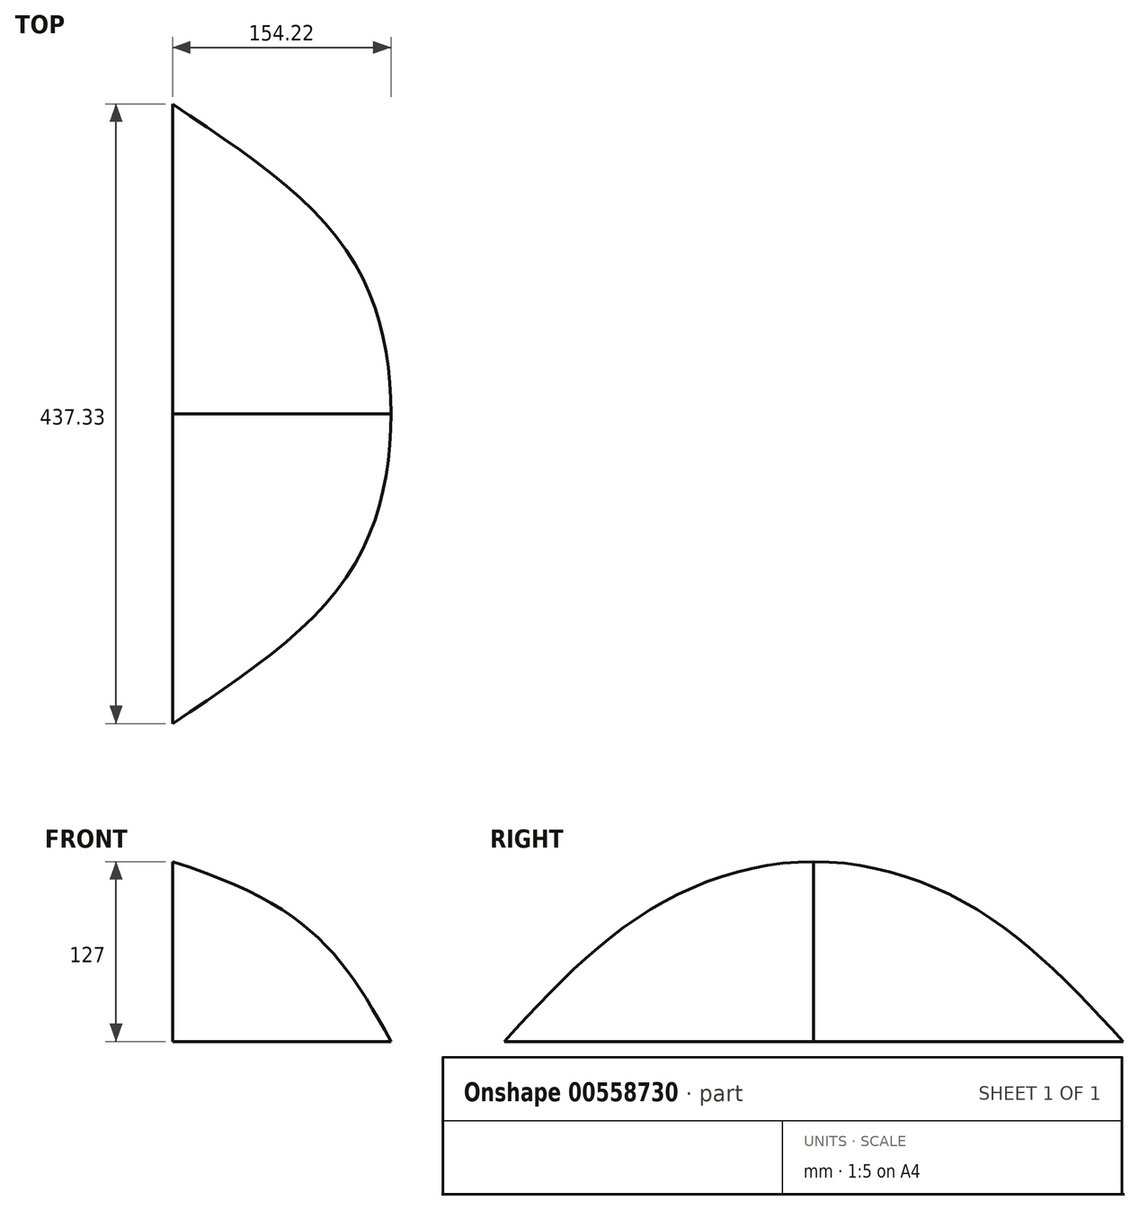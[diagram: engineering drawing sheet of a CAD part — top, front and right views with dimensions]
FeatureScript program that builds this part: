
annotation { "Feature Type Name" : "Feature", "Feature Type Description" : "" }
export const myFeature = defineFeature(function(context is Context, id is Id, definition is map)
    precondition{}
    {
        {
            var Q0;
            Q0=qCreatedBy(makeId("Top.planeOp"),FACE);
            var sketch = newSketch(context, id + "F0", { "sketchPlane" : qUnion([Q0])});
            skFitSpline(sketch, "E0", {"points": [v(0, 174.94) * mm, v(115.82, 81.22) * mm, v(154.22, -43.73) * mm], "startDerivative": vector(281.66, -68.02) * mm, "endDerivative": vector(-8.42, -224.14) * mm});
            skSolve(sketch);
        }
        {
            var Q0;
            Q0=qCreatedBy(makeId("Front.planeOp"),FACE);
            var Q1;
            Q1=sQuery(id+"F0.wireOp",VERTEX,"E0.end");
            cPlane(context, id + "F1", {"entities" : qUnion([Q0, Q1]), "cplaneType" : CPlaneType.PLANE_POINT, "offset" : 25.4 * mm, "width" : 152.4 * mm, "height" : 152.4 * mm});
        }
        {
            var Q0;
            Q0=qCreatedBy(id+"F1.planeOp",FACE);
            var sketch = newSketch(context, id + "F2", { "sketchPlane" : qUnion([Q0])});
            skLineSegment(sketch, "E1", {"start": v(154.22, 0) * mm, "end": v(0, 0) * mm});
            skLineSegment(sketch, "E2", {"start": v(0, 0) * mm, "end": v(0, 127) * mm});
            skFitSpline(sketch, "E3", {"points": [v(0, 127) * mm, v(154.22, 0) * mm], "startDerivative": vector(285.84, -90.22) * mm, "endDerivative": vector(103.03, -188.07) * mm});
            skSolve(sketch);
        }
        {
            var Q0;
            Q0=sQuery(id+"F0.wireOp",VERTEX,"E0.1.internal");
            var Q1;
            Q1=qCreatedBy(id+"F1.planeOp",FACE);
            cPlane(context, id + "F3", {"entities" : qUnion([Q0, Q1]), "cplaneType" : CPlaneType.PLANE_POINT, "offset" : 25.4 * mm, "width" : 152.4 * mm, "height" : 152.4 * mm});
        }
        {
            var Q0;
            Q0=qCreatedBy(makeId("Right.planeOp"),FACE);
            var sketch = newSketch(context, id + "F4", { "sketchPlane" : qUnion([Q0])});
            skFitSpline(sketch, "E4", {"points": [v(174.94, 0) * mm, v(-43.73, 127) * mm], "startDerivative": vector(-117.74, 161.24) * mm, "endDerivative": vector(-284.9, 0) * mm});
            skSolve(sketch);
        }
        {
            var Q0;
            Q0=qCreatedBy(id+"F3.planeOp",FACE);
            var sketch = newSketch(context, id + "F5", { "sketchPlane" : qUnion([Q0])});
            skFitSpline(sketch, "E5", {"points": [v(0, 87.07) * mm, v(49.88, 56.7) * mm, v(70.62, 34.97) * mm, v(115.82, 0) * mm], "startDerivative": vector(319.48, -90.5) * mm, "endDerivative": vector(119.36, -260.52) * mm});
            skLineSegment(sketch, "E6", {"start": v(115.82, 0) * mm, "end": v(0, 0) * mm});
            skLineSegment(sketch, "E7", {"start": v(0, 0) * mm, "end": v(0, 87.07) * mm});
            skSolve(sketch);
        }
        {
            var Q0;
            Q0=sQuery(id+"F2.wireOp",EDGE,"E3");
            var Q1;
            Q1=sQuery(id+"F5.wireOp",EDGE,"E5");
            var Q2;
            Q2=sQuery(id+"F0.wireOp",VERTEX,"E0.0.internal");
            var Q3;
            Q3=sQuery(id+"F0.wireOp",EDGE,"E0");
            loft(context, id + "F6", {"bodyType" : ToolBodyType.SURFACE, "startCondition" : LoftEndDerivativeType.NORMAL_TO_PROFILE, "startMagnitude" : 1, "wireProfilesArray" : [{ "wireProfileEntities" : qUnion([Q0]) }, { "wireProfileEntities" : qUnion([Q1]) }, { "wireProfileEntities" : qUnion([Q2]) }], "guidesArray" : [{ "guideEntities" : qUnion([Q3]), "guideDerivativeType" : LoftGuideDerivativeType.DEFAULT, "guideDerivativeMagnitude" : 1 }]});
        }
        {
            var Q0;
            Q0=makeQuery(id+"F6.opLoft","MID_CAP_EDGE",EDGE,{"disambiguationData":[OSD([sQuery(id+"F2.wireOp",VERTEX,"E3.start"),sQuery(id+"F2.wireOp",VERTEX,"E3.end"),sQuery(id+"F2.wireOp",EDGE,"E3")])],"capPos":0.0});
            cPoint(context, id + "F7", {"entities" : qUnion([Q0]), "parameter" : 0.5});
        }
        {
            var Q0;
            Q0=qCreatedBy(makeId("Front.planeOp"),FACE);
            var Q1;
            Q1 = qCreatedBy(id + "F7" ,VERTEX);
            cPlane(context, id + "F8", {"entities" : qUnion([Q0, Q1]), "cplaneType" : CPlaneType.PLANE_POINT, "offset" : 25.4 * mm, "width" : 152.4 * mm, "height" : 152.4 * mm});
        }
        {
            var Q0;
            Q0=makeQuery(id+"F6.opLoft","SWEPT_BODY",BODY,{"disambiguationData":[OSD([sQuery(id+"F0.wireOp",VERTEX,"E0.0.internal"),sQuery(id+"F2.wireOp",EDGE,"E3"),sQuery(id+"F5.wireOp",EDGE,"E5")])]});
            var Q1;
            Q1=qCreatedBy(id+"F8.planeOp",FACE);
            mirror(context, id + "F9", {"entities" : qUnion([Q0]), "mirrorPlane" : qUnion([Q1])});
        }
    });
